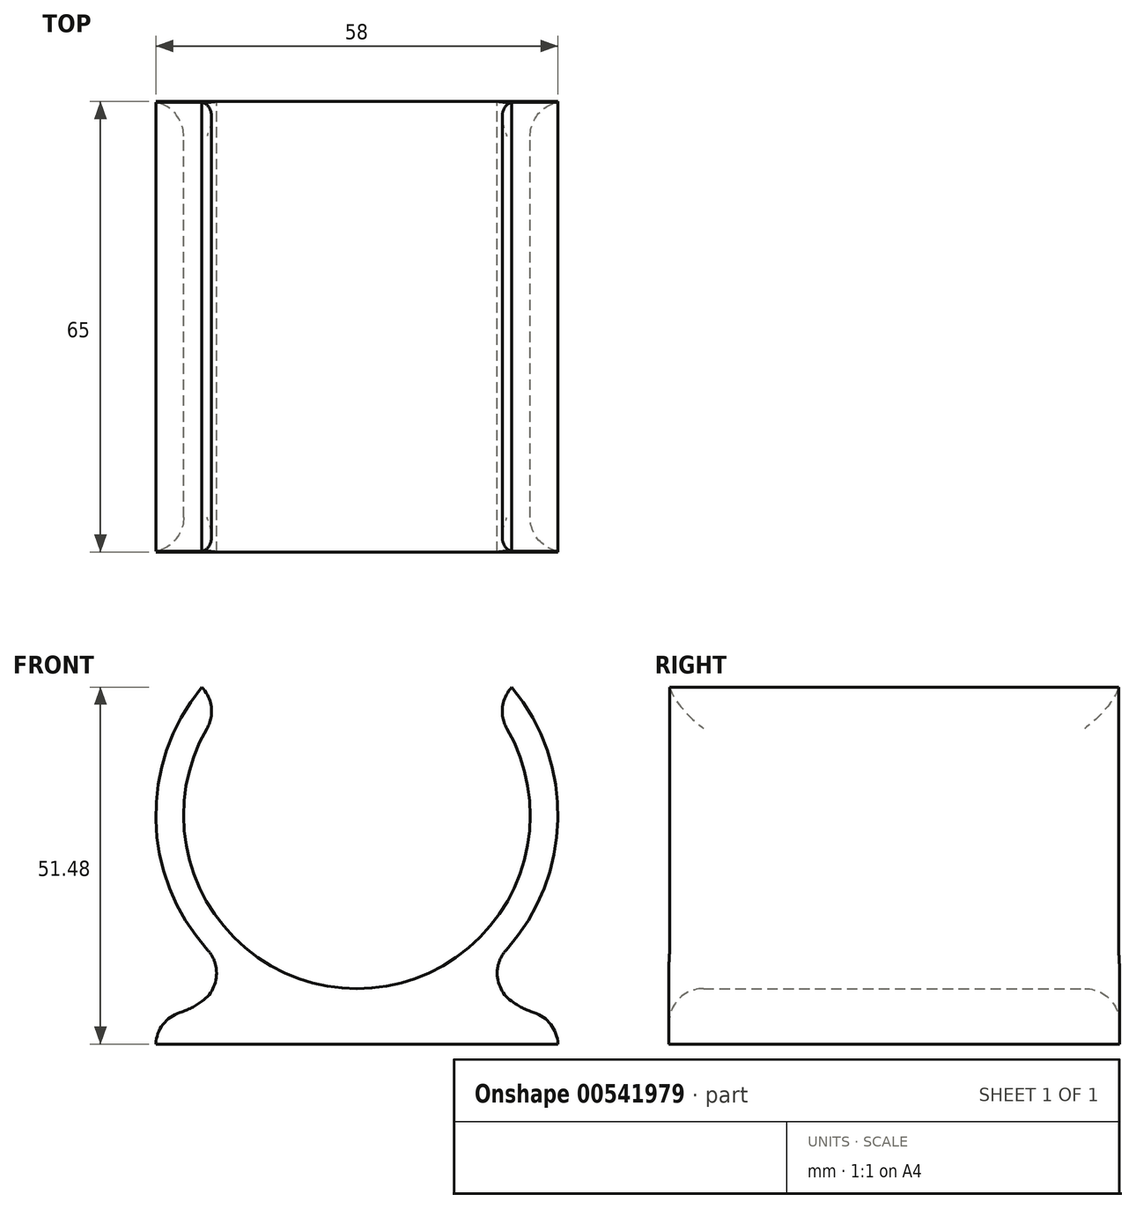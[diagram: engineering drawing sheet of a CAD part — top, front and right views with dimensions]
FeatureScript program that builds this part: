
annotation { "Feature Type Name" : "Feature", "Feature Type Description" : "" }
export const myFeature = defineFeature(function(context is Context, id is Id, definition is map)
    precondition{}
    {
        {
            var Q0;
            Q0=qCreatedBy(makeId("Front.planeOp"),FACE);
            var sketch = newSketch(context, id + "F0", { "sketchPlane" : qUnion([Q0])});
            skCircle(sketch, "E0", {"center": v(0, 0) * mm, "radius": 25 * mm});
            skCircle(sketch, "E1", {"center": v(0, 0) * mm, "radius": 29 * mm});
            skLineSegment(sketch, "E2", {"start": v(0, 0) * mm, "end": v(0, -29) * mm, "construction": true});
            skLineSegment(sketch, "E3", {"start": v(0, -29) * mm, "end": v(0, -33) * mm});
            skLineSegment(sketch, "E4", {"start": v(0, 0) * mm, "end": v(-29, 0) * mm, "construction": true});
            skLineSegment(sketch, "E5", {"start": v(-29, -29) * mm, "end": v(-29, -33) * mm});
            skLineSegment(sketch, "E6", {"start": v(0, 0) * mm, "end": v(29, 0) * mm, "construction": true});
            skLineSegment(sketch, "E7", {"start": v(29, -29) * mm, "end": v(29, -33) * mm});
            skLineSegment(sketch, "E8", {"start": v(0, -33) * mm, "end": v(-29, -33) * mm});
            skLineSegment(sketch, "E9", {"start": v(0, -33) * mm, "end": v(29, -33) * mm});
            skLineSegment(sketch, "E10", {"start": v(0, -29) * mm, "end": v(-29, -29) * mm});
            skLineSegment(sketch, "E11", {"start": v(0, -29) * mm, "end": v(29, -29) * mm});
            skLineSegment(sketch, "E12", {"start": v(-18.6, -22.25) * mm, "end": v(-18.6, -29) * mm, "construction": true});
            skLineSegment(sketch, "E13", {"start": v(18.6, -22.25) * mm, "end": v(18.6, -29) * mm, "construction": true});
            skArc(sketch, "E14", {"start": v(-29, -29) * mm, "mid": v(-22.8, -27.16) * mm, "end": v(-18.6, -22.25) * mm});
            skArc(sketch, "E15", {"start": v(18.6, -22.25) * mm, "mid": v(22.8, -27.16) * mm, "end": v(29, -29) * mm});
            skSolve(sketch);
        }
        {
            var Q0;
            Q0=makeQuery(id+"F0.imprint","IMPRINT",FACE,{"disambiguationData":[TD([[makeQuery(id+"F0.imprint","IMPRINT",EDGE,{"derivedFrom":sQuery(id+"F0.wireOp",EDGE,"E0")}),-1.0]])]});
            var Q1;
            {var subQ0=sQuery(id+"F0.wireOp",EDGE,"E10");Q1=makeQuery(id+"F0.imprint","IMPRINT",FACE,{"disambiguationData":[TD([[makeQuery(id+"F0.imprint","IMPRINT",EDGE,{"derivedFrom":subQ0}),-1.0]])]});}
            var Q2;
            {var subQ0=sQuery(id+"F0.wireOp",EDGE,"E11");Q2=makeQuery(id+"F0.imprint","IMPRINT",FACE,{"disambiguationData":[TD([[makeQuery(id+"F0.imprint","IMPRINT",EDGE,{"derivedFrom":subQ0}),1.0]])]});}
            var Q3;
            Q3=makeQuery(id+"F0.imprint","IMPRINT",FACE,{"disambiguationData":[TD([[makeQuery(id+"F0.imprint","IMPRINT",EDGE,{"derivedFrom":sQuery(id+"F0.wireOp",EDGE,"E3")}),-1.0]])]});
            var Q4;
            Q4=makeQuery(id+"F0.imprint","IMPRINT",FACE,{"disambiguationData":[TD([[makeQuery(id+"F0.imprint","IMPRINT",EDGE,{"derivedFrom":sQuery(id+"F0.wireOp",EDGE,"E3")}),1.0]])]});
            extrude(context, id + "F1", {"entities" : qUnion([Q0, Q1, Q2, Q3, Q4]), "depth" : 65 * mm, "offsetDistance" : 25 * mm});
        }
        {
            var Q0;
            Q0=qCreatedBy(makeId("Front.planeOp"),FACE);
            var sketch = newSketch(context, id + "F2", { "sketchPlane" : qUnion([Q0])});
            skLineSegment(sketch, "E16", {"start": v(0, 0) * mm, "end": v(-61.93, 51.2) * mm});
            skLineSegment(sketch, "E17", {"start": v(-61.93, 51.2) * mm, "end": v(61.93, 51.2) * mm});
            skLineSegment(sketch, "E18", {"start": v(61.93, 51.2) * mm, "end": v(0, 0) * mm});
            skSolve(sketch);
        }
        {
            var Q0;
            Q0 = qSketchRegion(id + "F2", true);
            extrude(context, id + "F3", {"entities" : qUnion([Q0]), "operationType" : NewBodyOperationType.REMOVE, "depth" : 70 * mm, "offsetDistance" : 25 * mm});
        }
        {
            var Q0;
            Q0=makeQuery(id+"F1.opExtrude","CAP_EDGE",EDGE,{"disambiguationData":[OSD([sQuery(id+"F0.wireOp",EDGE,"E0")])],"isStart":false});
            var Q1;
            Q1=makeQuery(id+"F1.opExtrude","CAP_EDGE",EDGE,{"disambiguationData":[OSD([sQuery(id+"F0.wireOp",EDGE,"E0")])],"isStart":true});
            var Q2;
            Q2=makeQuery(id+"F3.boolean.opBoolean","INTERSECT",EDGE,{"derivedFrom":[makeQuery(id+"F1.opExtrude","SWEPT_FACE",FACE,{"disambiguationData":[OSD([sQuery(id+"F0.wireOp",EDGE,"E0")])]}),makeQuery(id+"F3.opExtrude","SWEPT_FACE",FACE,{"disambiguationData":[OSD([sQuery(id+"F2.wireOp",EDGE,"E16")])]})]});
            var Q3;
            Q3=makeQuery(id+"F3.boolean.opBoolean","INTERSECT",EDGE,{"derivedFrom":[makeQuery(id+"F1.opExtrude","SWEPT_FACE",FACE,{"disambiguationData":[OSD([sQuery(id+"F0.wireOp",EDGE,"E0")])]}),makeQuery(id+"F3.opExtrude","SWEPT_FACE",FACE,{"disambiguationData":[OSD([sQuery(id+"F2.wireOp",EDGE,"E18")])]})]});
            var Q4;
            Q4=makeQuery(id+"F1.opExtrude","SWEPT_EDGE",EDGE,{"disambiguationData":[OSD([sQuery(id+"F0.wireOp",EDGE,"E5"),sQuery(id+"F0.wireOp",EDGE,"E10"),sQuery(id+"F0.wireOp",EDGE,"E14")])]});
            var Q5;
            Q5=makeQuery(id+"F1.opExtrude","SWEPT_EDGE",EDGE,{"disambiguationData":[OSD([sQuery(id+"F0.wireOp",EDGE,"E7"),sQuery(id+"F0.wireOp",EDGE,"E11"),sQuery(id+"F0.wireOp",EDGE,"E15")])]});
            fillet(context, id + "F4", {"entities" : qUnion([Q0, Q1, Q2, Q3, Q4, Q5]), "radius" : 5 * mm, "tangentPropagation" : true, "allowEdgeOverflow" : false});
        }
        {
            var Q0;
            Q0=makeQuery(id+"F1.opExtrude","SWEPT_EDGE",EDGE,{"disambiguationData":[OSD([sQuery(id+"F0.wireOp",EDGE,"E1"),sQuery(id+"F0.wireOp",EDGE,"E15")])]});
            var Q1;
            Q1=makeQuery(id+"F1.opExtrude","SWEPT_EDGE",EDGE,{"disambiguationData":[OSD([sQuery(id+"F0.wireOp",EDGE,"E1"),sQuery(id+"F0.wireOp",EDGE,"E14")])]});
            fillet(context, id + "F5", {"entities" : qUnion([Q0, Q1]), "radius" : 5 * mm, "tangentPropagation" : true, "allowEdgeOverflow" : false});
        }
    });
